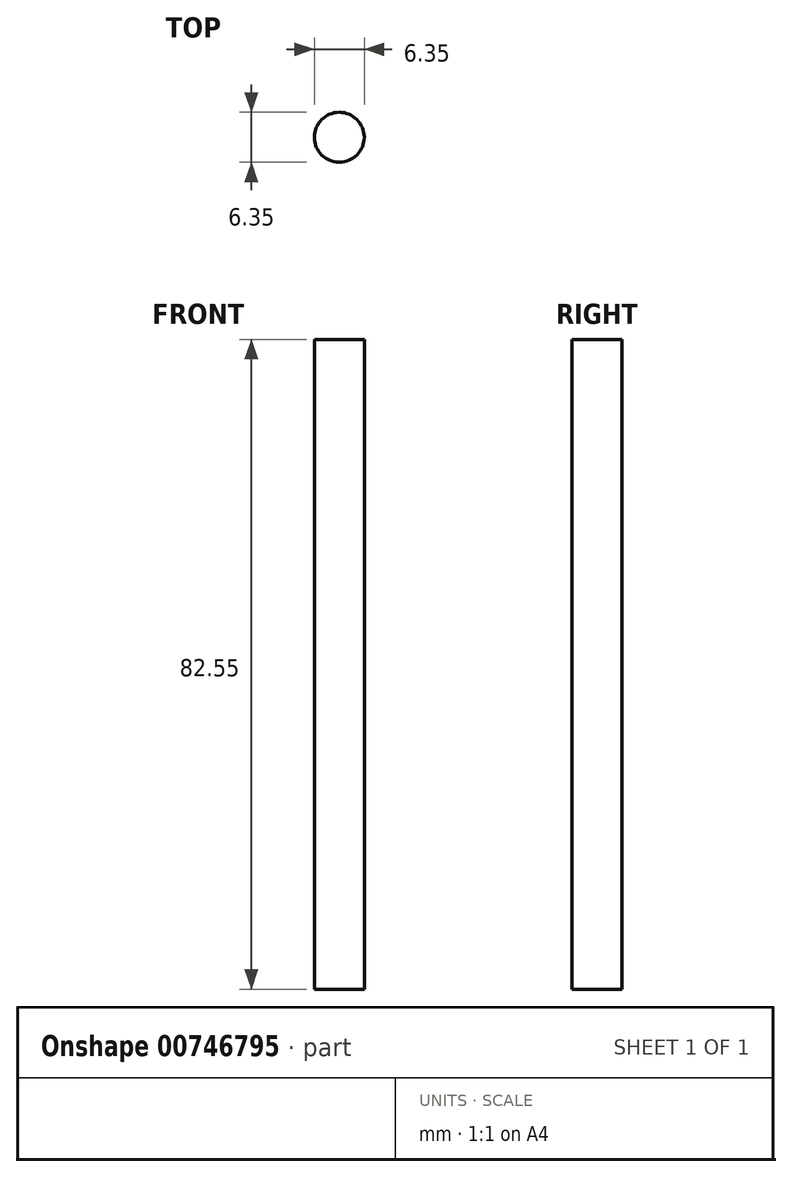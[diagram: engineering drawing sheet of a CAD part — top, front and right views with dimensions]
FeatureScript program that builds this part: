
annotation { "Feature Type Name" : "Feature", "Feature Type Description" : "" }
export const myFeature = defineFeature(function(context is Context, id is Id, definition is map)
    precondition{}
    {
        {
            var Q0;
            Q0=qCreatedBy(makeId("Top.planeOp"),FACE);
            var sketch = newSketch(context, id + "F0", { "sketchPlane" : qUnion([Q0])});
            skCircle(sketch, "E0", {"center": v(20.75, -24.9) * mm, "radius": 3.18 * mm});
            skSolve(sketch);
        }
        {
            var Q0;
            Q0=makeQuery(id+"F0.imprint","IMPRINT",FACE,{"disambiguationData":[TD([[makeQuery(id+"F0.imprint","IMPRINT",EDGE,{"derivedFrom":sQuery(id+"F0.wireOp",EDGE,"E0")}),1.0]])]});
            extrude(context, id + "F1", {"entities" : qUnion([Q0]), "depth" : 82.55 * mm, "offsetDistance" : 25.4 * mm});
        }
    });
